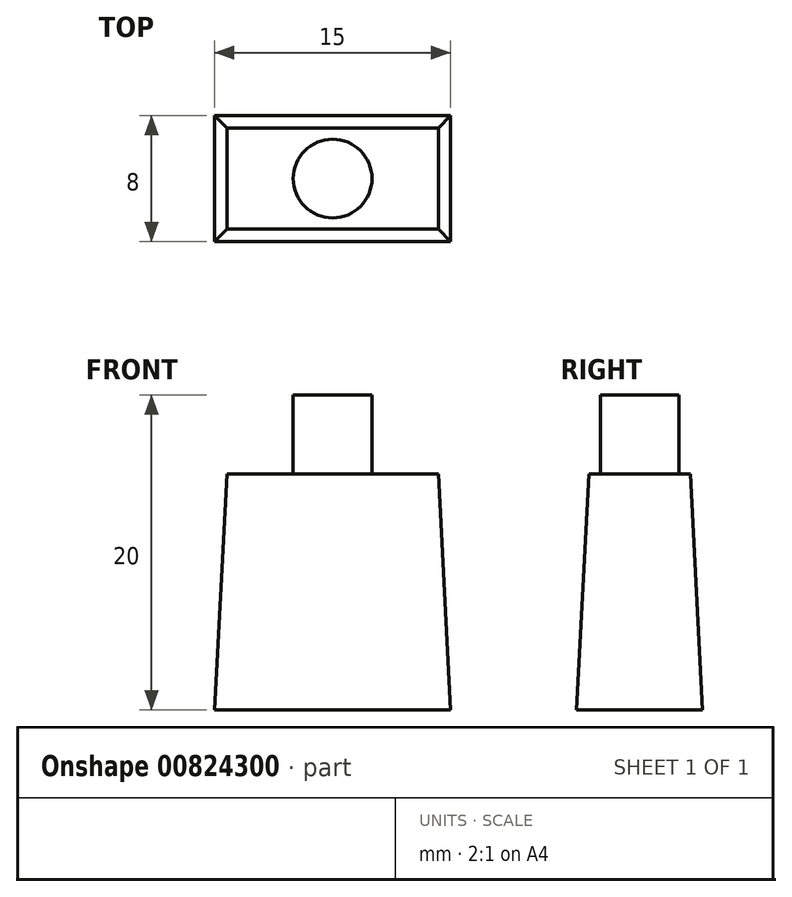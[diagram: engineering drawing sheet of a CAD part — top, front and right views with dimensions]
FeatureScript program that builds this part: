
annotation { "Feature Type Name" : "Feature", "Feature Type Description" : "" }
export const myFeature = defineFeature(function(context is Context, id is Id, definition is map)
    precondition{}
    {
        {
            var Q0;
            Q0=qCreatedBy(makeId("Top.planeOp"),FACE);
            var sketch = newSketch(context, id + "F0", { "sketchPlane" : qUnion([Q0])});
            skLineSegment(sketch, "E0.bottom", {"start": v(7.5, -4) * mm, "end": v(-7.5, -4) * mm});
            skLineSegment(sketch, "E0.top", {"start": v(7.5, 4) * mm, "end": v(-7.5, 4) * mm});
            skLineSegment(sketch, "E0.left", {"start": v(7.5, -4) * mm, "end": v(7.5, 4) * mm});
            skLineSegment(sketch, "E0.right", {"start": v(-7.5, -4) * mm, "end": v(-7.5, 4) * mm});
            skPoint(sketch, "E0.middle", {"position": v(0, 0) * mm});
            skSolve(sketch);
        }
        {
            var Q0;
            Q0 = qSketchRegion(id + "F0", true);
            extrude(context, id + "F1", {"entities" : qUnion([Q0]), "depth" : 15 * mm, "offsetDistance" : 25 * mm, "hasDraft" : true, "draftAngle" : 3 * degree, "draftPullDirection" : true});
        }
        {
            var Q0;
            Q0=makeQuery(id+"F1.opExtrude","CAP_FACE",FACE,{"disambiguationData":[OSD([sQuery(id+"F0.wireOp",EDGE,"E0.bottom"),sQuery(id+"F0.wireOp",EDGE,"E0.top"),sQuery(id+"F0.wireOp",EDGE,"E0.left"),sQuery(id+"F0.wireOp",EDGE,"E0.right")])],"isStart":false});
            var sketch = newSketch(context, id + "F2", { "sketchPlane" : qUnion([Q0])});
            skCircle(sketch, "E1", {"center": v(0, 0) * mm, "radius": 2.5 * mm});
            skSolve(sketch);
        }
        {
            var Q0;
            Q0 = qSketchRegion(id + "F2", true);
            extrude(context, id + "F3", {"entities" : qUnion([Q0]), "operationType" : NewBodyOperationType.ADD, "depth" : 5 * mm, "offsetDistance" : 25 * mm});
        }
    });
